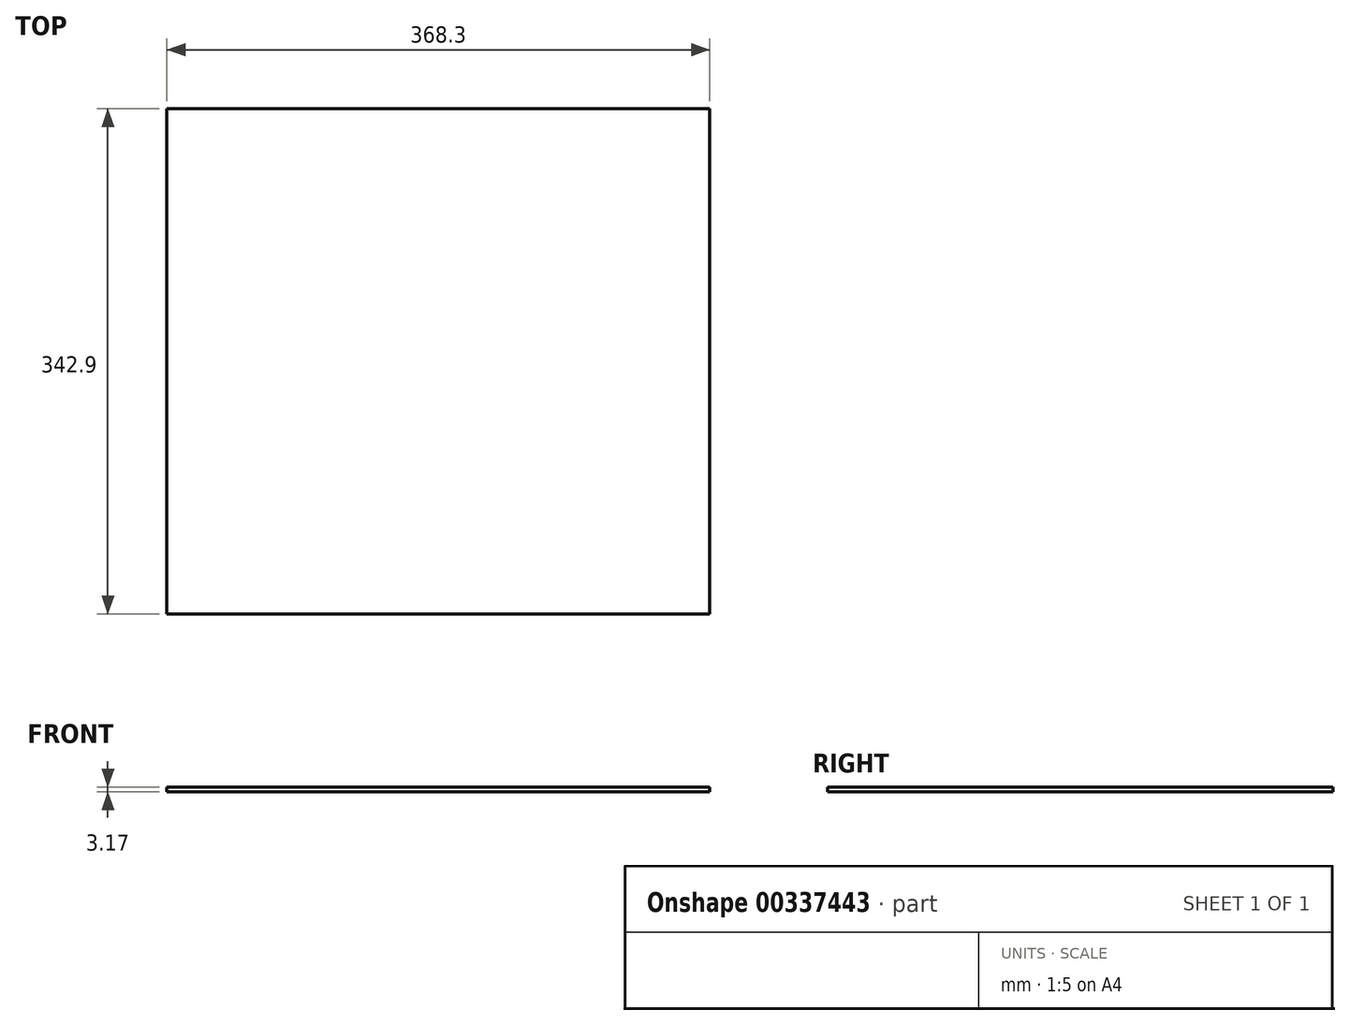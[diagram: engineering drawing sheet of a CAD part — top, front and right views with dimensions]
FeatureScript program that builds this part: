
annotation { "Feature Type Name" : "Feature", "Feature Type Description" : "" }
export const myFeature = defineFeature(function(context is Context, id is Id, definition is map)
    precondition{}
    {
        {
            var Q0;
            Q0=qCreatedBy(makeId("Top.planeOp"),FACE);
            var sketch = newSketch(context, id + "F0", { "sketchPlane" : qUnion([Q0])});
            skLineSegment(sketch, "E0.bottom", {"start": v(-184.15, 171.45) * mm, "end": v(184.15, 171.45) * mm});
            skLineSegment(sketch, "E0.top", {"start": v(-184.15, -171.45) * mm, "end": v(184.15, -171.45) * mm});
            skLineSegment(sketch, "E0.left", {"start": v(-184.15, 171.45) * mm, "end": v(-184.15, -171.45) * mm});
            skLineSegment(sketch, "E0.right", {"start": v(184.15, 171.45) * mm, "end": v(184.15, -171.45) * mm});
            skPoint(sketch, "E0.middle", {"position": v(0, 0) * mm});
            skSolve(sketch);
        }
        {
            var Q0;
            Q0=makeQuery(id+"F0.imprint","IMPRINT",FACE,{"disambiguationData":[TD([[makeQuery(id+"F0.imprint","IMPRINT",EDGE,{"derivedFrom":sQuery(id+"F0.wireOp",EDGE,"E0.bottom")}),-1.0]])]});
            extrude(context, id + "F1", {"entities" : qUnion([Q0]), "depth" : 3.17 * mm});
        }
    });
